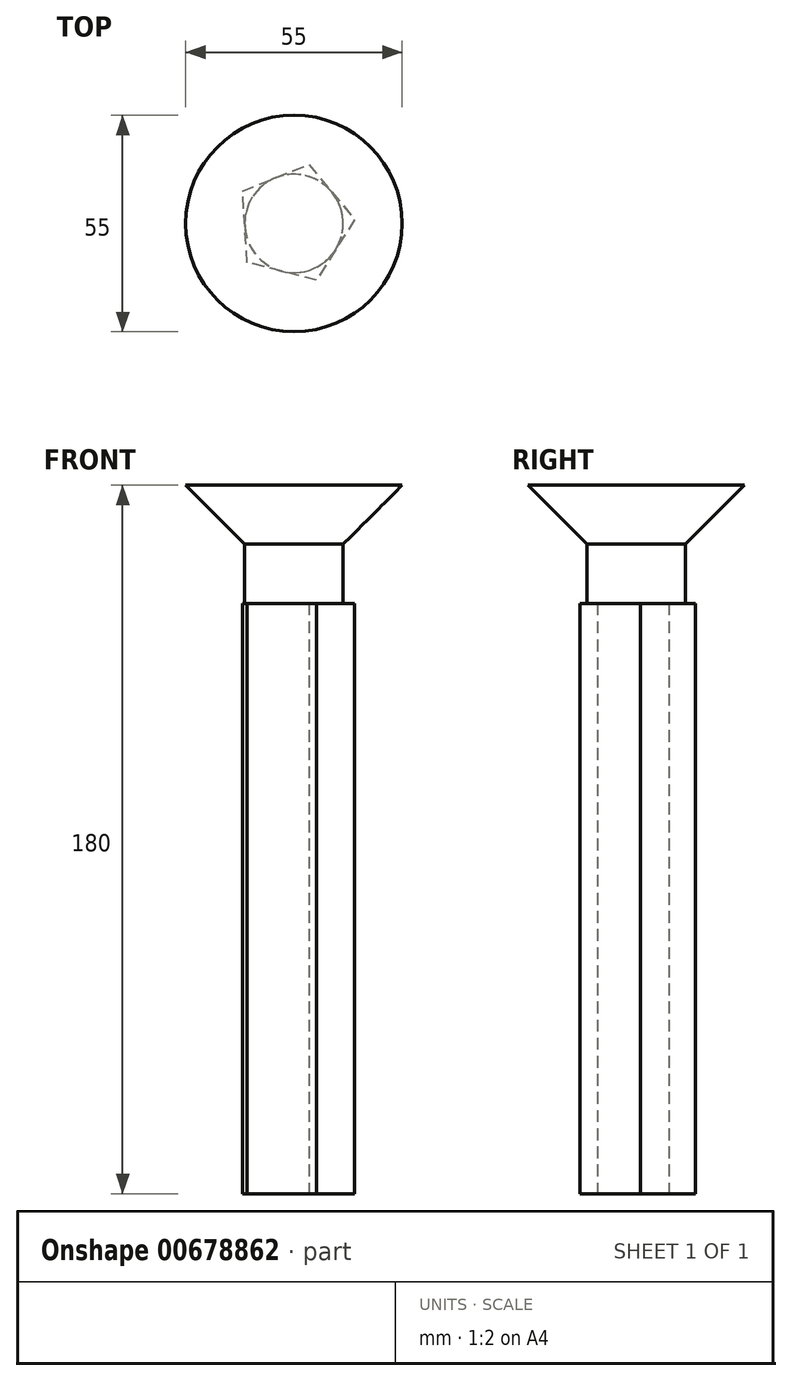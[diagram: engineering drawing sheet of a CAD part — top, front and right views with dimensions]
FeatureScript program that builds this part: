
annotation { "Feature Type Name" : "Feature", "Feature Type Description" : "" }
export const myFeature = defineFeature(function(context is Context, id is Id, definition is map)
    precondition{}
    {
        {
            var Q0;
            Q0=qCreatedBy(makeId("Top.planeOp"),FACE);
            var sketch = newSketch(context, id + "F0", { "sketchPlane" : qUnion([Q0])});
            skLineSegment(sketch, "E0.0", {"start": v(3.8, 14.98) * mm, "end": v(15.42, 1.02) * mm});
            skLineSegment(sketch, "E0.1", {"start": v(15.42, 1.02) * mm, "end": v(5.73, -14.35) * mm});
            skLineSegment(sketch, "E0.2", {"start": v(5.73, -14.35) * mm, "end": v(-11.88, -9.89) * mm});
            skLineSegment(sketch, "E0.3", {"start": v(-11.88, -9.89) * mm, "end": v(-13.07, 8.24) * mm});
            skLineSegment(sketch, "E0.4", {"start": v(-13.07, 8.24) * mm, "end": v(3.8, 14.98) * mm});
            skSolve(sketch);
        }
        {
            var Q0;
            Q0=makeQuery(id+"F0.imprint","IMPRINT",FACE,{"disambiguationData":[TD([[makeQuery(id+"F0.imprint","IMPRINT",EDGE,{"derivedFrom":sQuery(id+"F0.wireOp",EDGE,"E0.0")}),-1.0]])]});
            var Q1;
            Q1=sQuery(id+"FIAGVctAvDIoumU.wireOp",EDGE,"2d9964be-070d-4756-9806-facb3aff7fa9.0");
            var Q2;
            Q2=sQuery(id+"FIAGVctAvDIoumU.wireOp",EDGE,"2d9964be-070d-4756-9806-facb3aff7fa9.1");
            var Q3;
            Q3=sQuery(id+"FIAGVctAvDIoumU.wireOp",EDGE,"2d9964be-070d-4756-9806-facb3aff7fa9.2");
            var Q4;
            Q4=sQuery(id+"FIAGVctAvDIoumU.wireOp",EDGE,"2d9964be-070d-4756-9806-facb3aff7fa9.3");
            var Q5;
            Q5=sQuery(id+"FIAGVctAvDIoumU.wireOp",EDGE,"2d9964be-070d-4756-9806-facb3aff7fa9.4");
            var Q6;
            Q6=sQuery(id+"FIAGVctAvDIoumU.wireOp",EDGE,"2d9964be-070d-4756-9806-facb3aff7fa9.5");
            extrude(context, id + "F1", {"entities" : qUnion([Q0]), "surfaceEntities" : qUnion([Q1, Q2, Q3, Q4, Q5, Q6]), "depth" : 150 * mm, "offsetDistance" : 25 * mm});
        }
        {
            var Q0;
            Q0=makeQuery(id+"F1.opExtrude","CAP_FACE",FACE,{"disambiguationData":[OSD([sQuery(id+"F0.wireOp",EDGE,"E0.0"),sQuery(id+"F0.wireOp",EDGE,"E0.1"),sQuery(id+"F0.wireOp",EDGE,"E0.2"),sQuery(id+"F0.wireOp",EDGE,"E0.3"),sQuery(id+"F0.wireOp",EDGE,"E0.4")])],"isStart":false});
            var sketch = newSketch(context, id + "F2", { "sketchPlane" : qUnion([Q0])});
            skCircle(sketch, "E1", {"center": v(0, 0) * mm, "radius": 12.5 * mm});
            skSolve(sketch);
        }
        {
            var Q0;
            {var subQ0=sQuery(id+"F2.wireOp",EDGE,"E1");var subQ4=makeQuery(id+"F2.imprint","INTERSECT",VERTEX,{"derivedFrom":[makeQuery(id+"F1.opExtrude","CAP_EDGE",EDGE,{"disambiguationData":[OSD([sQuery(id+"F0.wireOp",EDGE,"E0.4")])],"isStart":false}),subQ0]});Q0=makeQuery(id+"F2.imprint","IMPRINT",FACE,{"disambiguationData":[TD([[makeQuery(id+"F2.imprint","IMPRINT",EDGE,{"disambiguationData":[TD([[subQ4,1.0]])],"derivedFrom":subQ0}),1.0]])]});}
            extrude(context, id + "F3", {"entities" : qUnion([Q0]), "operationType" : NewBodyOperationType.ADD, "depth" : 15 * mm, "offsetDistance" : 25 * mm});
        }
        {
            var Q0;
            Q0=makeQuery(id+"F3.opExtrude","CAP_FACE",FACE,{"disambiguationData":[OSD([sQuery(id+"F2.wireOp",EDGE,"E1")])],"isStart":false});
            extrude(context, id + "F4", {"entities" : qUnion([Q0]), "operationType" : NewBodyOperationType.ADD, "depth" : 15 * mm, "offsetDistance" : 25 * mm, "hasDraft" : true, "draftAngle" : 45 * degree});
        }
    });
